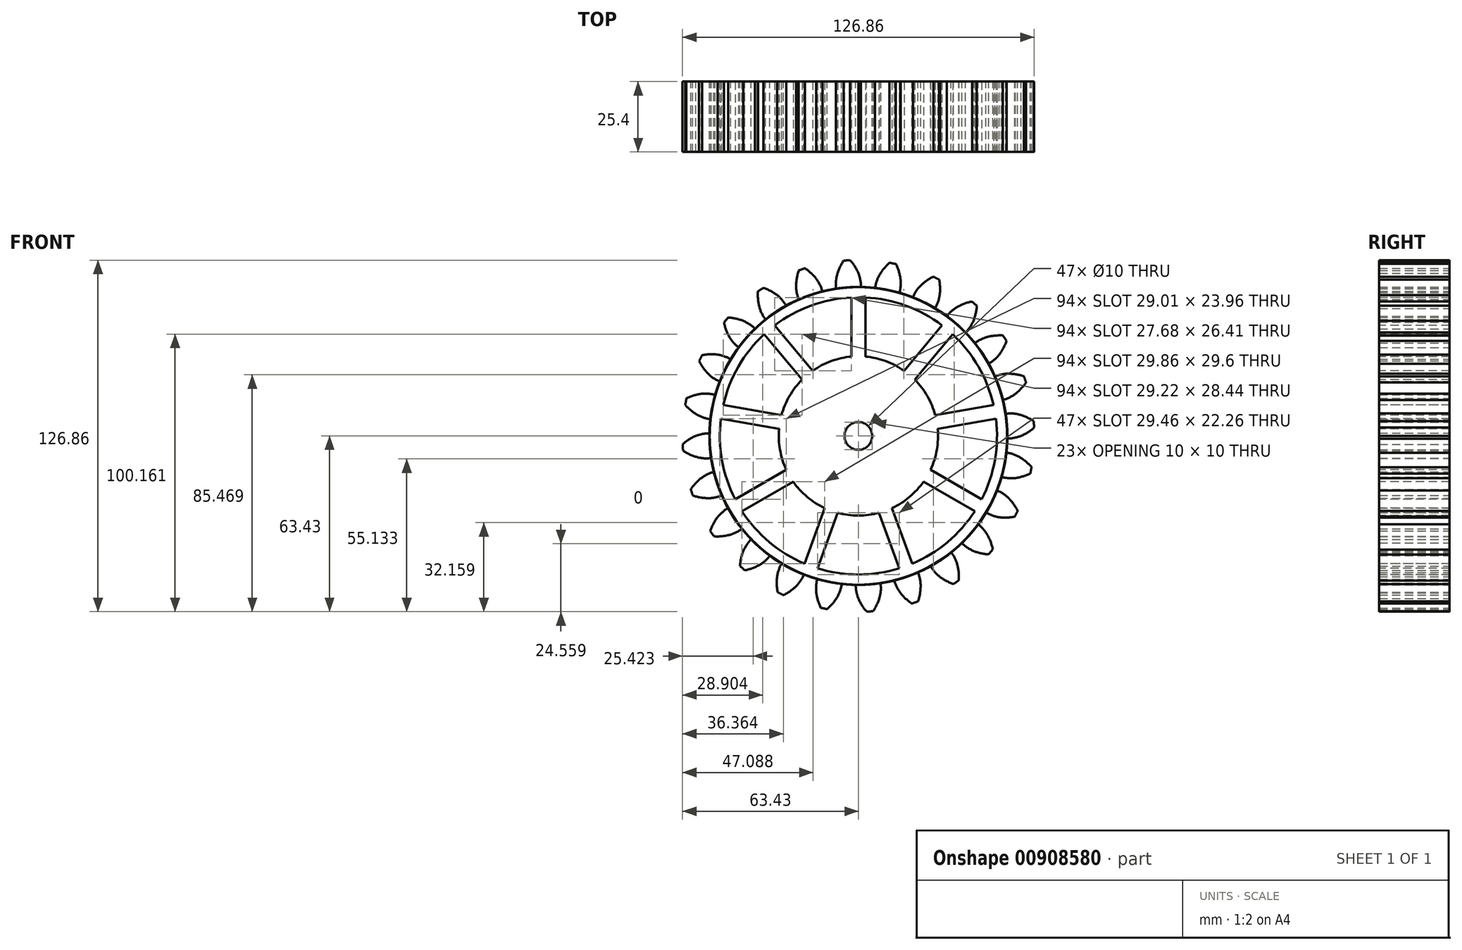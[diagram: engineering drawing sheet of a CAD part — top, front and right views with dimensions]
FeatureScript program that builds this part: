
annotation { "Feature Type Name" : "Feature", "Feature Type Description" : "" }
export const myFeature = defineFeature(function(context is Context, id is Id, definition is map)
    precondition{}
    {
        {
            var Q0;
            Q0=qCreatedBy(makeId("Front.planeOp"),FACE);
            var sketch = newSketch(context, id + "F0", { "sketchPlane" : qUnion([Q0])});
            skCircle(sketch, "E0", {"center": v(0, 0) * mm, "radius": 63.5 * mm, "construction": true});
            skCircle(sketch, "E1", {"center": v(0, 0) * mm, "radius": 58.67 * mm, "construction": true});
            skCircle(sketch, "E2", {"center": v(0, 0) * mm, "radius": 53.72 * mm});
            skLineSegment(sketch, "E3", {"start": v(0, 0) * mm, "end": v(0, 113.9) * mm, "construction": true});
            skLineSegment(sketch, "E4", {"start": v(0, 0) * mm, "end": v(-7.6, 116.01) * mm, "construction": true});
            skLineSegment(sketch, "E5", {"start": v(0, 58.67) * mm, "end": v(-127.04, 58.67) * mm, "construction": true});
            skLineSegment(sketch, "E6", {"start": v(0, 58.67) * mm, "end": v(-129.75, 11.45) * mm, "construction": true});
            skCircle(sketch, "E7", {"center": v(0, 0) * mm, "radius": 55.14 * mm, "construction": true});
            skCircle(sketch, "E8", {"center": v(0, 58.67) * mm, "radius": 14.6 * mm, "construction": true});
            skCircle(sketch, "E9", {"center": v(-13.63, 53.42) * mm, "radius": 14.6 * mm, "construction": true});
            skArc(sketch, "E10", {"start": v(0, 58.67) * mm, "mid": v(-1.28, 61.19) * mm, "end": v(-2.99, 63.43) * mm});
            skArc(sketch, "E11", {"start": v(0.97, 53.71) * mm, "mid": v(0.7, 56.23) * mm, "end": v(0, 58.67) * mm});
            skArc(sketch, "E12", {"start": v(0, 58.67) * mm, "mid": v(-1.31, 61.17) * mm, "end": v(-2.99, 63.43) * mm});
            skArc(sketch, "E13", {"start": v(0.97, 53.71) * mm, "mid": v(0.75, 56.24) * mm, "end": v(0, 58.67) * mm});
            skArc(sketch, "E14.MirrorCS", {"start": v(-7.66, 58.17) * mm, "mid": v(-6.69, 60.82) * mm, "end": v(-5.32, 63.28) * mm});
            skArc(sketch, "E15.MirrorCS", {"start": v(-7.98, 53.13) * mm, "mid": v(-8.09, 55.67) * mm, "end": v(-7.66, 58.17) * mm});
            skArc(sketch, "E16", {"start": v(-5.32, 63.28) * mm, "mid": v(-4.15, 63.32) * mm, "end": v(-2.99, 63.43) * mm});
            skArc(sketch, "E17", {"start": v(-204.28, -7.2) * mm, "mid": v(-205.56, -4.7) * mm, "end": v(-207.27, -2.45) * mm});
            skArc(sketch, "E18", {"start": v(-203.3, -12.17) * mm, "mid": v(-203.58, -9.65) * mm, "end": v(-204.28, -7.2) * mm});
            skArc(sketch, "E19", {"start": v(-204.28, -7.2) * mm, "mid": v(-205.59, -4.71) * mm, "end": v(-207.27, -2.45) * mm});
            skArc(sketch, "E20", {"start": v(-203.3, -12.17) * mm, "mid": v(-203.53, -9.64) * mm, "end": v(-204.28, -7.2) * mm});
            skArc(sketch, "E21.MirrorCS", {"start": v(-211.94, -7.7) * mm, "mid": v(-210.96, -5.07) * mm, "end": v(-209.6, -2.6) * mm});
            skArc(sketch, "E22.MirrorCS", {"start": v(-212.25, -12.76) * mm, "mid": v(-212.36, -10.21) * mm, "end": v(-211.94, -7.7) * mm});
            skArc(sketch, "E23", {"start": v(-209.6, -2.6) * mm, "mid": v(-208.43, -2.56) * mm, "end": v(-207.27, -2.45) * mm});
            skSolve(sketch);
        }
        {
            var Q0;
            {var subQ0=sQuery(id+"F0.wireOp",EDGE,"E2");var subQ2=makeQuery(id+"F0.imprint","INTERSECT",VERTEX,{"derivedFrom":[subQ0,sQuery(id+"F0.wireOp",EDGE,"E15.MirrorCS")]});Q0=makeQuery(id+"F0.imprint","IMPRINT",FACE,{"disambiguationData":[TD([[makeQuery(id+"F0.imprint","IMPRINT",EDGE,{"disambiguationData":[TD([[subQ2,1.0]])],"derivedFrom":subQ0}),1.0]])]});}
            var Q1;
            {var subQ0=sQuery(id+"F0.wireOp",EDGE,"E11");Q1=makeQuery(id+"F0.imprint","IMPRINT",FACE,{"disambiguationData":[TD([[makeQuery(id+"F0.imprint","IMPRINT",EDGE,{"derivedFrom":subQ0}),1.0]])]});}
            extrude(context, id + "F1", {"entities" : qUnion([Q0, Q1]), "depth" : 25.4 * mm, "offsetDistance" : 25.4 * mm});
        }
        {
            var Q0;
            Q0=makeQuery(id+"F1.opExtrude","SWEPT_BODY",BODY,{"disambiguationData":[OSD([sQuery(id+"F0.wireOp",EDGE,"E2"),sQuery(id+"F0.wireOp",EDGE,"E11"),sQuery(id+"F0.wireOp",EDGE,"E12"),sQuery(id+"F0.wireOp",EDGE,"E14.MirrorCS"),sQuery(id+"F0.wireOp",EDGE,"E15.MirrorCS"),sQuery(id+"F0.wireOp",EDGE,"E16")])]});
            var Q1;
            Q1=makeQuery(id+"F1.opExtrude","SWEPT_FACE",FACE,{"disambiguationData":[OSD([sQuery(id+"F0.wireOp",EDGE,"E2")])]});
            circularPattern(context, id + "F2", {"entities" : qUnion([Q0]), "axis" : qUnion([Q1]), "angle" : 15 * degree, "instanceCount" : 24, "isCentered" : true});
        }
        {
            var Q0;
            Q0=makeQuery(id+"F1.opExtrude","CAP_FACE",FACE,{"disambiguationData":[OSD([sQuery(id+"F0.wireOp",EDGE,"E2"),sQuery(id+"F0.wireOp",EDGE,"E11"),sQuery(id+"F0.wireOp",EDGE,"E12"),sQuery(id+"F0.wireOp",EDGE,"E14.MirrorCS"),sQuery(id+"F0.wireOp",EDGE,"E15.MirrorCS"),sQuery(id+"F0.wireOp",EDGE,"E16")])],"isStart":false});
            var sketch = newSketch(context, id + "F3", { "sketchPlane" : qUnion([Q0])});
            skCircle(sketch, "E24", {"center": v(0, 0) * mm, "radius": 28.72 * mm});
            skCircle(sketch, "E25", {"center": v(0, 0) * mm, "radius": 50 * mm});
            skLineSegment(sketch, "E26", {"start": v(0, 50) * mm, "end": v(2.5, 49.94) * mm});
            skLineSegment(sketch, "E27", {"start": v(2.5, 49.94) * mm, "end": v(2.5, 28.61) * mm});
            skLineSegment(sketch, "E28", {"start": v(-2.5, 49.94) * mm, "end": v(-2.5, 28.61) * mm});
            skPoint(sketch, "E29.start.orphan", {"position": v(0, 28.72) * mm});
            skLineSegment(sketch, "E30.1.0", {"start": v(-30.18, 39.86) * mm, "end": v(-16.48, 23.53) * mm});
            skLineSegment(sketch, "E30.1.1", {"start": v(-34.01, 36.65) * mm, "end": v(-20.3, 20.31) * mm});
            skLineSegment(sketch, "E30.2.0", {"start": v(-48.74, 11.13) * mm, "end": v(-27.74, 7.43) * mm});
            skLineSegment(sketch, "E30.2.1", {"start": v(-49.61, 6.2) * mm, "end": v(-28.61, 2.5) * mm});
            skLineSegment(sketch, "E31.2.3.0", {"start": v(-44.5, -22.8) * mm, "end": v(-26.03, -12.14) * mm});
            skLineSegment(sketch, "E31.3.3.0", {"start": v(-42, -27.13) * mm, "end": v(-23.53, -16.47) * mm});
            skLineSegment(sketch, "E31.2.4.0", {"start": v(-19.43, -46.07) * mm, "end": v(-12.14, -26.03) * mm});
            skLineSegment(sketch, "E31.3.4.0", {"start": v(-14.73, -47.78) * mm, "end": v(-7.44, -27.74) * mm});
            skLineSegment(sketch, "E31.2.5.0", {"start": v(14.73, -47.78) * mm, "end": v(7.44, -27.74) * mm});
            skLineSegment(sketch, "E31.3.5.0", {"start": v(19.43, -46.07) * mm, "end": v(12.14, -26.03) * mm});
            skLineSegment(sketch, "E31.2.6.0", {"start": v(42, -27.13) * mm, "end": v(23.53, -16.47) * mm});
            skLineSegment(sketch, "E31.3.6.0", {"start": v(44.5, -22.8) * mm, "end": v(26.03, -12.14) * mm});
            skLineSegment(sketch, "E32.2.7.0", {"start": v(49.61, 6.2) * mm, "end": v(28.61, 2.5) * mm});
            skLineSegment(sketch, "E32.3.7.0", {"start": v(48.74, 11.13) * mm, "end": v(27.74, 7.43) * mm});
            skLineSegment(sketch, "E32.2.8.0", {"start": v(34.01, 36.65) * mm, "end": v(20.3, 20.31) * mm});
            skLineSegment(sketch, "E32.3.8.0", {"start": v(30.18, 39.86) * mm, "end": v(16.48, 23.53) * mm});
            skSolve(sketch);
        }
        {
            var Q0;
            {var subQ0=sQuery(id+"F3.wireOp",EDGE,"E28");Q0=makeQuery(id+"F3.imprint","IMPRINT",FACE,{"disambiguationData":[TD([[makeQuery(id+"F3.imprint","IMPRINT",EDGE,{"derivedFrom":subQ0}),-1.0]])]});}
            var Q1;
            {var subQ0=sQuery(id+"F3.wireOp",EDGE,"E27");Q1=makeQuery(id+"F3.imprint","IMPRINT",FACE,{"disambiguationData":[TD([[makeQuery(id+"F3.imprint","IMPRINT",EDGE,{"derivedFrom":subQ0}),1.0]])]});}
            var Q2;
            {var subQ0=sQuery(id+"F3.wireOp",EDGE,"E32.3.7.0");Q2=makeQuery(id+"F3.imprint","IMPRINT",FACE,{"disambiguationData":[TD([[makeQuery(id+"F3.imprint","IMPRINT",EDGE,{"derivedFrom":subQ0}),-1.0]])]});}
            var Q3;
            {var subQ0=sQuery(id+"F3.wireOp",EDGE,"E31.3.6.0");Q3=makeQuery(id+"F3.imprint","IMPRINT",FACE,{"disambiguationData":[TD([[makeQuery(id+"F3.imprint","IMPRINT",EDGE,{"derivedFrom":subQ0}),-1.0]])]});}
            var Q4;
            {var subQ0=sQuery(id+"F3.wireOp",EDGE,"E30.1.1");Q4=makeQuery(id+"F3.imprint","IMPRINT",FACE,{"disambiguationData":[TD([[makeQuery(id+"F3.imprint","IMPRINT",EDGE,{"derivedFrom":subQ0}),-1.0]])]});}
            var Q5;
            {var subQ0=sQuery(id+"F3.wireOp",EDGE,"E30.2.1");Q5=makeQuery(id+"F3.imprint","IMPRINT",FACE,{"disambiguationData":[TD([[makeQuery(id+"F3.imprint","IMPRINT",EDGE,{"derivedFrom":subQ0}),-1.0]])]});}
            var Q6;
            {var subQ0=sQuery(id+"F3.wireOp",EDGE,"E31.3.3.0");Q6=makeQuery(id+"F3.imprint","IMPRINT",FACE,{"disambiguationData":[TD([[makeQuery(id+"F3.imprint","IMPRINT",EDGE,{"derivedFrom":subQ0}),-1.0]])]});}
            var Q7;
            {var subQ0=sQuery(id+"F3.wireOp",EDGE,"E31.3.4.0");Q7=makeQuery(id+"F3.imprint","IMPRINT",FACE,{"disambiguationData":[TD([[makeQuery(id+"F3.imprint","IMPRINT",EDGE,{"derivedFrom":subQ0}),-1.0]])]});}
            var Q8;
            {var subQ0=sQuery(id+"F3.wireOp",EDGE,"E31.3.5.0");Q8=makeQuery(id+"F3.imprint","IMPRINT",FACE,{"disambiguationData":[TD([[makeQuery(id+"F3.imprint","IMPRINT",EDGE,{"derivedFrom":subQ0}),-1.0]])]});}
            extrude(context, id + "F4", {"entities" : qUnion([Q0, Q1, Q2, Q3, Q4, Q5, Q6, Q7, Q8]), "operationType" : NewBodyOperationType.REMOVE, "oppositeDirection" : true, "depth" : 50 * mm, "offsetDistance" : 25 * mm});
        }
        {
            var Q0;
            Q0=makeQuery(id+"F1.opExtrude","CAP_FACE",FACE,{"disambiguationData":[OSD([sQuery(id+"F0.wireOp",EDGE,"E2"),sQuery(id+"F0.wireOp",EDGE,"E11"),sQuery(id+"F0.wireOp",EDGE,"E12"),sQuery(id+"F0.wireOp",EDGE,"E14.MirrorCS"),sQuery(id+"F0.wireOp",EDGE,"E15.MirrorCS"),sQuery(id+"F0.wireOp",EDGE,"E16")])],"isStart":true});
            var sketch = newSketch(context, id + "F5", { "sketchPlane" : qUnion([Q0])});
            skCircle(sketch, "E33", {"center": v(0, 0) * mm, "radius": 5 * mm});
            skSolve(sketch);
        }
        {
            var Q0;
            Q0=makeQuery(id+"F5.imprint","IMPRINT",FACE,{"disambiguationData":[TD([[makeQuery(id+"F5.imprint","IMPRINT",EDGE,{"derivedFrom":sQuery(id+"F5.wireOp",EDGE,"E33")}),1.0]])]});
            extrude(context, id + "F6", {"entities" : qUnion([Q0]), "operationType" : NewBodyOperationType.REMOVE, "oppositeDirection" : true, "depth" : 50 * mm, "offsetDistance" : 25 * mm});
        }
    });
